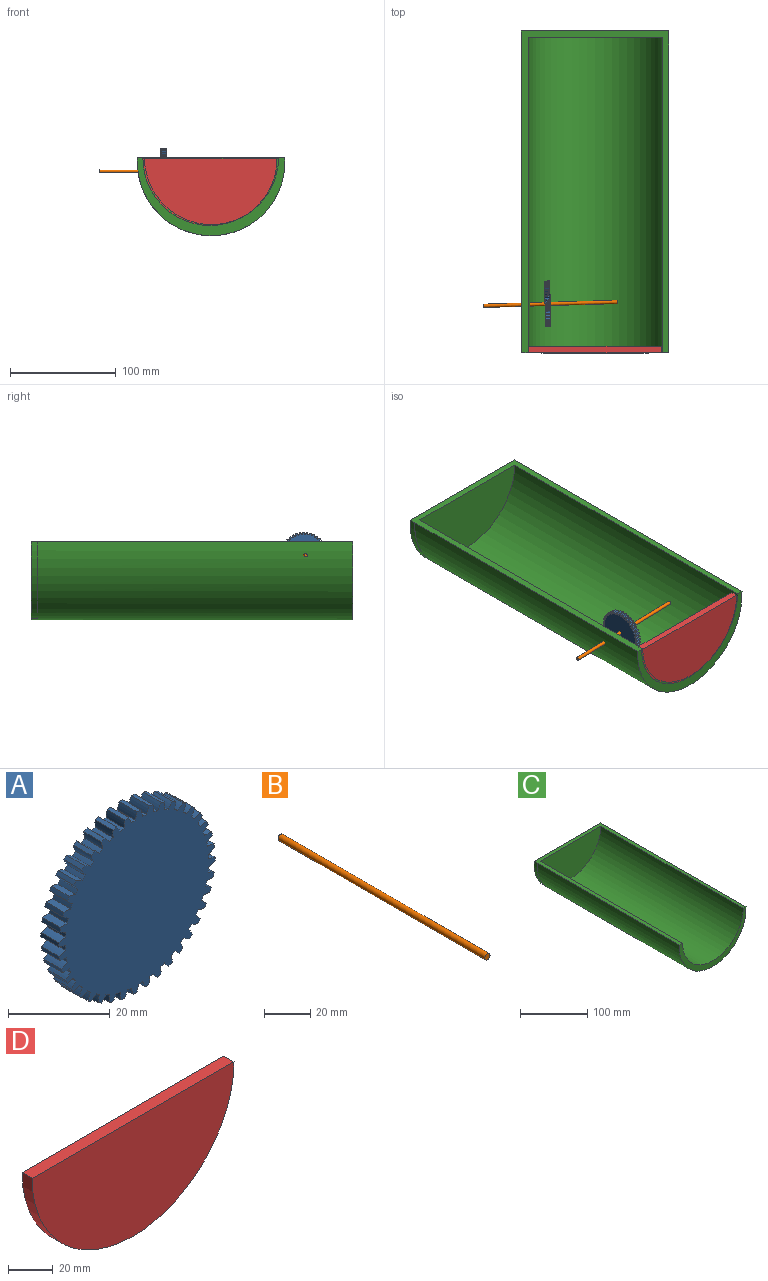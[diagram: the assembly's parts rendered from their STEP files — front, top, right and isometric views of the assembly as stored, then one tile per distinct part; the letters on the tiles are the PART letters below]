
ASSEMBLY  parts=4 mates=2
PART A: 162 faces, bbox 43.5x5x43.5 mm
  f0: cylinder r=20mm len=5mm, axis (0,1,0), area 5.8mm2, adj f40,f41,f42,f161
  f1: cylinder r=20mm len=5mm, axis (0,1,0), area 5.8mm2, adj f40,f41,f158,f159
  f2: cylinder r=20mm len=5mm, axis (0,1,0), area 5.8mm2, adj f40,f41,f155,f156
  f3: cylinder r=20mm len=5mm, axis (0,1,0), area 5.8mm2, adj f40,f41,f152,f153
  f4: cylinder r=20mm len=5mm, axis (0,1,0), area 5.8mm2, adj f40,f41,f149,f150
  f5: cylinder r=20mm len=5mm, axis (0,1,0), area 5.8mm2, adj f40,f41,f146,f147
  f6: cylinder r=20mm len=5mm, axis (0,1,0), area 5.8mm2, adj f40,f41,f143,f144
  f7: cylinder r=20mm len=5mm, axis (0,1,0), area 5.8mm2, adj f40,f41,f140,f141
  f8: cylinder r=20mm len=5mm, axis (0,1,0), area 5.8mm2, adj f40,f41,f137,f138
  f9: cylinder r=20mm len=5mm, axis (0,1,0), area 5.8mm2, adj f40,f41,f134,f135
  f10: cylinder r=20mm len=5mm, axis (0,1,0), area 5.8mm2, adj f40,f41,f131,f132
  f11: cylinder r=20mm len=5mm, axis (0,1,0), area 5.8mm2, adj f40,f41,f128,f129
  f12: cylinder r=20mm len=5mm, axis (0,1,0), area 5.8mm2, adj f40,f41,f125,f126
  f13: cylinder r=20mm len=5mm, axis (0,1,0), area 5.8mm2, adj f40,f41,f122,f123
  f14: cylinder r=20mm len=5mm, axis (0,1,0), area 5.8mm2, adj f40,f41,f119,f120
  f15: cylinder r=20mm len=5mm, axis (0,1,0), area 5.8mm2, adj f40,f41,f116,f117
  f16: cylinder r=20mm len=5mm, axis (0,1,0), area 5.8mm2, adj f40,f41,f113,f114
  f17: cylinder r=20mm len=5mm, axis (0,1,0), area 5.8mm2, adj f40,f41,f110,f111
  f18: cylinder r=20mm len=5mm, axis (0,1,0), area 5.8mm2, adj f40,f41,f107,f108
  f19: cylinder r=20mm len=5mm, axis (0,1,0), area 5.8mm2, adj f40,f41,f104,f105
  f20: cylinder r=20mm len=5mm, axis (0,1,0), area 5.8mm2, adj f40,f41,f101,f102
  f21: cylinder r=20mm len=5mm, axis (0,1,0), area 5.8mm2, adj f40,f41,f98,f99
  f22: cylinder r=20mm len=5mm, axis (0,1,0), area 5.8mm2, adj f40,f41,f95,f96
  f23: cylinder r=20mm len=5mm, axis (0,1,0), area 5.8mm2, adj f40,f41,f92,f93
  f24: cylinder r=20mm len=5mm, axis (0,1,0), area 5.8mm2, adj f40,f41,f89,f90
  f25: cylinder r=20mm len=5mm, axis (0,1,0), area 5.8mm2, adj f40,f41,f86,f87
  f26: cylinder r=20mm len=5mm, axis (0,1,0), area 5.8mm2, adj f40,f41,f83,f84
  f27: cylinder r=20mm len=5mm, axis (0,1,0), area 5.8mm2, adj f40,f41,f80,f81
  f28: cylinder r=20mm len=5mm, axis (0,1,0), area 5.8mm2, adj f40,f41,f77,f78
  f29: cylinder r=20mm len=5mm, axis (0,1,0), area 5.8mm2, adj f40,f41,f74,f75
  f30: cylinder r=20mm len=5mm, axis (0,1,0), area 5.8mm2, adj f40,f41,f71,f72
  f31: cylinder r=20mm len=5mm, axis (0,1,0), area 5.8mm2, adj f40,f41,f68,f69
  f32: cylinder r=20mm len=5mm, axis (0,1,0), area 5.8mm2, adj f40,f41,f65,f66
  f33: cylinder r=20mm len=5mm, axis (0,1,0), area 5.8mm2, adj f40,f41,f62,f63
  f34: cylinder r=20mm len=5mm, axis (0,1,0), area 5.8mm2, adj f40,f41,f59,f60
  f35: cylinder r=20mm len=5mm, axis (0,1,0), area 5.8mm2, adj f40,f41,f56,f57
  f36: cylinder r=20mm len=5mm, axis (0,1,0), area 5.8mm2, adj f40,f41,f53,f54
  f37: cylinder r=20mm len=5mm, axis (0,1,0), area 5.8mm2, adj f40,f41,f50,f51
  f38: cylinder r=20mm len=5mm, axis (0,1,0), area 5.8mm2, adj f40,f41,f47,f48
  f39: cylinder r=20mm len=5mm, axis (0,1,0), area 5.8mm2, adj f40,f41,f44,f45
  f40: plane 43.5x43.5mm, normal (0,-1,0), area 1366.6mm2, adj f0,f1,f2,f3,f4,f5,f6,f7
  f41: plane 43.5x43.5mm, normal (0,1,0), area 1366.6mm2, adj f0,f1,f2,f3,f4,f5,f6,f7
  f42: cylinder r=8.16mm len=5mm, axis (0,1,0), area 9.2mm2, adj f0,f40,f41,f43
  f43: cylinder r=21.75mm len=5mm, axis (0,1,0), area 5.1mm2, adj f40,f41,f42,f44
  f44: cylinder r=8.16mm len=5mm, axis (0,1,0), area 9.2mm2, adj f39,f40,f41,f43
  f45: cylinder r=8.16mm len=5mm, axis (0,1,0), area 9.2mm2, adj f39,f40,f41,f46
  f46: cylinder r=21.75mm len=5mm, axis (0,1,0), area 5.1mm2, adj f40,f41,f45,f47
  f47: cylinder r=8.16mm len=5mm, axis (0,1,0), area 9.2mm2, adj f38,f40,f41,f46
  f48: cylinder r=8.16mm len=5mm, axis (0,1,0), area 9.2mm2, adj f38,f40,f41,f49
  f49: cylinder r=21.75mm len=5mm, axis (0,1,0), area 5.1mm2, adj f40,f41,f48,f50
  f50: cylinder r=8.16mm len=5mm, axis (0,1,0), area 9.2mm2, adj f37,f40,f41,f49
  f51: cylinder r=8.16mm len=5mm, axis (0,1,0), area 9.2mm2, adj f37,f40,f41,f52
  f52: cylinder r=21.75mm len=5mm, axis (0,1,0), area 5.1mm2, adj f40,f41,f51,f53
  f53: cylinder r=8.16mm len=5mm, axis (0,1,0), area 9.2mm2, adj f36,f40,f41,f52
  f54: cylinder r=8.16mm len=5mm, axis (0,1,0), area 9.2mm2, adj f36,f40,f41,f55
  f55: cylinder r=21.75mm len=5mm, axis (0,1,0), area 5.1mm2, adj f40,f41,f54,f56
  f56: cylinder r=8.16mm len=5mm, axis (0,1,0), area 9.2mm2, adj f35,f40,f41,f55
  f57: cylinder r=8.16mm len=5mm, axis (0,1,0), area 9.2mm2, adj f35,f40,f41,f58
  f58: cylinder r=21.75mm len=5mm, axis (0,1,0), area 5.1mm2, adj f40,f41,f57,f59
  f59: cylinder r=8.16mm len=5mm, axis (0,1,0), area 9.2mm2, adj f34,f40,f41,f58
  f60: cylinder r=8.16mm len=5mm, axis (0,1,0), area 9.2mm2, adj f34,f40,f41,f61
  f61: cylinder r=21.75mm len=5mm, axis (0,1,0), area 5.1mm2, adj f40,f41,f60,f62
  f62: cylinder r=8.16mm len=5mm, axis (0,1,0), area 9.2mm2, adj f33,f40,f41,f61
  f63: cylinder r=8.16mm len=5mm, axis (0,1,0), area 9.2mm2, adj f33,f40,f41,f64
  f64: cylinder r=21.75mm len=5mm, axis (0,1,0), area 5.1mm2, adj f40,f41,f63,f65
  f65: cylinder r=8.16mm len=5mm, axis (0,1,0), area 9.2mm2, adj f32,f40,f41,f64
  f66: cylinder r=8.16mm len=5mm, axis (0,1,0), area 9.2mm2, adj f32,f40,f41,f67
  f67: cylinder r=21.75mm len=5mm, axis (0,1,0), area 5.1mm2, adj f40,f41,f66,f68
  f68: cylinder r=8.16mm len=5mm, axis (0,1,0), area 9.2mm2, adj f31,f40,f41,f67
  f69: cylinder r=8.16mm len=5mm, axis (0,1,0), area 9.2mm2, adj f31,f40,f41,f70
  f70: cylinder r=21.75mm len=5mm, axis (0,1,0), area 5.1mm2, adj f40,f41,f69,f71
  f71: cylinder r=8.16mm len=5mm, axis (0,1,0), area 9.2mm2, adj f30,f40,f41,f70
  f72: cylinder r=8.16mm len=5mm, axis (0,1,0), area 9.2mm2, adj f30,f40,f41,f73
  f73: cylinder r=21.75mm len=5mm, axis (0,1,0), area 5.1mm2, adj f40,f41,f72,f74
  f74: cylinder r=8.16mm len=5mm, axis (0,1,0), area 9.2mm2, adj f29,f40,f41,f73
  f75: cylinder r=8.16mm len=5mm, axis (0,1,0), area 9.2mm2, adj f29,f40,f41,f76
  f76: cylinder r=21.75mm len=5mm, axis (0,1,0), area 5.1mm2, adj f40,f41,f75,f77
  f77: cylinder r=8.16mm len=5mm, axis (0,1,0), area 9.2mm2, adj f28,f40,f41,f76
  f78: cylinder r=8.16mm len=5mm, axis (0,1,0), area 9.2mm2, adj f28,f40,f41,f79
  f79: cylinder r=21.75mm len=5mm, axis (0,1,0), area 5.1mm2, adj f40,f41,f78,f80
  f80: cylinder r=8.16mm len=5mm, axis (0,1,0), area 9.2mm2, adj f27,f40,f41,f79
  f81: cylinder r=8.16mm len=5mm, axis (0,1,0), area 9.2mm2, adj f27,f40,f41,f82
  f82: cylinder r=21.75mm len=5mm, axis (0,1,0), area 5.1mm2, adj f40,f41,f81,f83
  f83: cylinder r=8.16mm len=5mm, axis (0,1,0), area 9.2mm2, adj f26,f40,f41,f82
  f84: cylinder r=8.16mm len=5mm, axis (0,1,0), area 9.2mm2, adj f26,f40,f41,f85
  f85: cylinder r=21.75mm len=5mm, axis (0,1,0), area 5.1mm2, adj f40,f41,f84,f86
  f86: cylinder r=8.16mm len=5mm, axis (0,1,0), area 9.2mm2, adj f25,f40,f41,f85
  f87: cylinder r=8.16mm len=5mm, axis (0,1,0), area 9.2mm2, adj f25,f40,f41,f88
  f88: cylinder r=21.75mm len=5mm, axis (0,1,0), area 5.1mm2, adj f40,f41,f87,f89
  f89: cylinder r=8.16mm len=5mm, axis (0,1,0), area 9.2mm2, adj f24,f40,f41,f88
  f90: cylinder r=8.16mm len=5mm, axis (0,1,0), area 9.2mm2, adj f24,f40,f41,f91
  f91: cylinder r=21.75mm len=5mm, axis (0,1,0), area 5.1mm2, adj f40,f41,f90,f92
  f92: cylinder r=8.16mm len=5mm, axis (0,1,0), area 9.2mm2, adj f23,f40,f41,f91
  f93: cylinder r=8.16mm len=5mm, axis (0,1,0), area 9.2mm2, adj f23,f40,f41,f94
  f94: cylinder r=21.75mm len=5mm, axis (0,1,0), area 5.1mm2, adj f40,f41,f93,f95
  f95: cylinder r=8.16mm len=5mm, axis (0,1,0), area 9.2mm2, adj f22,f40,f41,f94
  f96: cylinder r=8.16mm len=5mm, axis (0,1,0), area 9.2mm2, adj f22,f40,f41,f97
  f97: cylinder r=21.75mm len=5mm, axis (0,1,0), area 5.1mm2, adj f40,f41,f96,f98
  f98: cylinder r=8.16mm len=5mm, axis (0,1,0), area 9.2mm2, adj f21,f40,f41,f97
  f99: cylinder r=8.16mm len=5mm, axis (0,1,0), area 9.2mm2, adj f21,f40,f41,f100
  f100: cylinder r=21.75mm len=5mm, axis (0,1,0), area 5.1mm2, adj f40,f41,f99,f101
  f101: cylinder r=8.16mm len=5mm, axis (0,1,0), area 9.2mm2, adj f20,f40,f41,f100
  f102: cylinder r=8.16mm len=5mm, axis (0,1,0), area 9.2mm2, adj f20,f40,f41,f103
  f103: cylinder r=21.75mm len=5mm, axis (0,1,0), area 5.1mm2, adj f40,f41,f102,f104
  f104: cylinder r=8.16mm len=5mm, axis (0,1,0), area 9.2mm2, adj f19,f40,f41,f103
  f105: cylinder r=8.16mm len=5mm, axis (0,1,0), area 9.2mm2, adj f19,f40,f41,f106
  f106: cylinder r=21.75mm len=5mm, axis (0,1,0), area 5.1mm2, adj f40,f41,f105,f107
  f107: cylinder r=8.16mm len=5mm, axis (0,1,0), area 9.2mm2, adj f18,f40,f41,f106
  f108: cylinder r=8.16mm len=5mm, axis (0,1,0), area 9.2mm2, adj f18,f40,f41,f109
  f109: cylinder r=21.75mm len=5mm, axis (0,1,0), area 5.1mm2, adj f40,f41,f108,f110
  f110: cylinder r=8.16mm len=5mm, axis (0,1,0), area 9.2mm2, adj f17,f40,f41,f109
  f111: cylinder r=8.16mm len=5mm, axis (0,1,0), area 9.2mm2, adj f17,f40,f41,f112
  f112: cylinder r=21.75mm len=5mm, axis (0,1,0), area 5.1mm2, adj f40,f41,f111,f113
  f113: cylinder r=8.16mm len=5mm, axis (0,1,0), area 9.2mm2, adj f16,f40,f41,f112
  f114: cylinder r=8.16mm len=5mm, axis (0,1,0), area 9.2mm2, adj f16,f40,f41,f115
  f115: cylinder r=21.75mm len=5mm, axis (0,1,0), area 5.1mm2, adj f40,f41,f114,f116
  f116: cylinder r=8.16mm len=5mm, axis (0,1,0), area 9.2mm2, adj f15,f40,f41,f115
  f117: cylinder r=8.16mm len=5mm, axis (0,1,0), area 9.2mm2, adj f15,f40,f41,f118
  f118: cylinder r=21.75mm len=5mm, axis (0,1,0), area 5.1mm2, adj f40,f41,f117,f119
  f119: cylinder r=8.16mm len=5mm, axis (0,1,0), area 9.2mm2, adj f14,f40,f41,f118
  f120: cylinder r=8.16mm len=5mm, axis (0,1,0), area 9.2mm2, adj f14,f40,f41,f121
  f121: cylinder r=21.75mm len=5mm, axis (0,1,0), area 5.1mm2, adj f40,f41,f120,f122
  f122: cylinder r=8.16mm len=5mm, axis (0,1,0), area 9.2mm2, adj f13,f40,f41,f121
  f123: cylinder r=8.16mm len=5mm, axis (0,1,0), area 9.2mm2, adj f13,f40,f41,f124
  f124: cylinder r=21.75mm len=5mm, axis (0,1,0), area 5.1mm2, adj f40,f41,f123,f125
  f125: cylinder r=8.16mm len=5mm, axis (0,1,0), area 9.2mm2, adj f12,f40,f41,f124
  f126: cylinder r=8.16mm len=5mm, axis (0,1,0), area 9.2mm2, adj f12,f40,f41,f127
  f127: cylinder r=21.75mm len=5mm, axis (0,1,0), area 5.1mm2, adj f40,f41,f126,f128
  f128: cylinder r=8.16mm len=5mm, axis (0,1,0), area 9.2mm2, adj f11,f40,f41,f127
  f129: cylinder r=8.16mm len=5mm, axis (0,1,0), area 9.2mm2, adj f11,f40,f41,f130
  f130: cylinder r=21.75mm len=5mm, axis (0,1,0), area 5.1mm2, adj f40,f41,f129,f131
  f131: cylinder r=8.16mm len=5mm, axis (0,1,0), area 9.2mm2, adj f10,f40,f41,f130
  f132: cylinder r=8.16mm len=5mm, axis (0,1,0), area 9.2mm2, adj f10,f40,f41,f133
  f133: cylinder r=21.75mm len=5mm, axis (0,1,0), area 5.1mm2, adj f40,f41,f132,f134
  f134: cylinder r=8.16mm len=5mm, axis (0,1,0), area 9.2mm2, adj f9,f40,f41,f133
  f135: cylinder r=8.16mm len=5mm, axis (0,1,0), area 9.2mm2, adj f9,f40,f41,f136
  f136: cylinder r=21.75mm len=5mm, axis (0,1,0), area 5.1mm2, adj f40,f41,f135,f137
  f137: cylinder r=8.16mm len=5mm, axis (0,1,0), area 9.2mm2, adj f8,f40,f41,f136
  f138: cylinder r=8.16mm len=5mm, axis (0,1,0), area 9.2mm2, adj f8,f40,f41,f139
  f139: cylinder r=21.75mm len=5mm, axis (0,1,0), area 5.1mm2, adj f40,f41,f138,f140
  f140: cylinder r=8.16mm len=5mm, axis (0,1,0), area 9.2mm2, adj f7,f40,f41,f139
  f141: cylinder r=8.16mm len=5mm, axis (0,1,0), area 9.2mm2, adj f7,f40,f41,f142
  f142: cylinder r=21.75mm len=5mm, axis (0,1,0), area 5.1mm2, adj f40,f41,f141,f143
  f143: cylinder r=8.16mm len=5mm, axis (0,1,0), area 9.2mm2, adj f6,f40,f41,f142
  f144: cylinder r=8.16mm len=5mm, axis (0,1,0), area 9.2mm2, adj f6,f40,f41,f145
  f145: cylinder r=21.75mm len=5mm, axis (0,1,0), area 5.1mm2, adj f40,f41,f144,f146
  f146: cylinder r=8.16mm len=5mm, axis (0,1,0), area 9.2mm2, adj f5,f40,f41,f145
  f147: cylinder r=8.16mm len=5mm, axis (0,1,0), area 9.2mm2, adj f5,f40,f41,f148
  f148: cylinder r=21.75mm len=5mm, axis (0,1,0), area 5.1mm2, adj f40,f41,f147,f149
  f149: cylinder r=8.16mm len=5mm, axis (0,1,0), area 9.2mm2, adj f4,f40,f41,f148
  f150: cylinder r=8.16mm len=5mm, axis (0,1,0), area 9.2mm2, adj f4,f40,f41,f151
  f151: cylinder r=21.75mm len=5mm, axis (0,1,0), area 5.1mm2, adj f40,f41,f150,f152
  f152: cylinder r=8.16mm len=5mm, axis (0,1,0), area 9.2mm2, adj f3,f40,f41,f151
  f153: cylinder r=8.16mm len=5mm, axis (0,1,0), area 9.2mm2, adj f3,f40,f41,f154
  f154: cylinder r=21.75mm len=5mm, axis (0,1,0), area 5.1mm2, adj f40,f41,f153,f155
  f155: cylinder r=8.16mm len=5mm, axis (0,1,0), area 9.2mm2, adj f2,f40,f41,f154
  f156: cylinder r=8.16mm len=5mm, axis (0,1,0), area 9.2mm2, adj f2,f40,f41,f157
  f157: cylinder r=21.75mm len=5mm, axis (0,1,0), area 5.1mm2, adj f40,f41,f156,f158
  f158: cylinder r=8.16mm len=5mm, axis (0,1,0), area 9.2mm2, adj f1,f40,f41,f157
  f159: cylinder r=8.16mm len=5mm, axis (0,1,0), area 9.2mm2, adj f1,f40,f41,f160
  f160: cylinder r=21.75mm len=5mm, axis (0,1,0), area 5.1mm2, adj f40,f41,f159,f161
  f161: cylinder r=8.16mm len=5mm, axis (0,1,0), area 9.2mm2, adj f0,f40,f41,f160
PART B: 3 faces, bbox 3.1x127x3.1 mm
  f0: cylinder r=1.57mm len=127mm, axis (0,1,0), area 1256.6mm2, adj f1,f2
  f1: plane 3.15x3.15mm, normal (0,-1,0), area 7.8mm2, adj f0
  f2: plane 3.15x3.15mm, normal (0,1,0), area 7.8mm2, adj f0
PART C: 8 faces, bbox 139.9x304.8x73.8 mm
  f0: cylinder r=69.85mm len=304.8mm, axis (0,1,0), area 68683.6mm2, adj f1,f3,f4,f6,f7
  f1: plane 304.8x139.71mm, normal (0,0,1), area 4609.9mm2, adj f0,f2,f3,f4,f5,f6,f7
  f2: cylinder r=63.5mm len=298.45mm, axis (0,1,0), area 59388.5mm2, adj f1,f3,f5
  f3: plane 139.7x73.84mm, normal (0,-1,0), area 1918.4mm2, adj f0,f1,f2
  f4: plane 139.94x73.84mm, normal (0,1,0), area 8234.9mm2, adj f0,f1,f6
  f5: plane 127x63.25mm, normal (0,-1,0), area 6302mm2, adj f1,f2
  f6: cylinder r=69.85mm len=72.42mm, axis (0,1,0), area 633.8mm2, adj f0,f1,f4,f7
  f7: plane 72.42x56.09mm, normal (0,-1,0), area 14.5mm2, adj f0,f1,f6
PART D: 4 faces, bbox 127x6.4x63.3 mm
  f0: plane 127x6.35mm, normal (0,0,1), area 806.4mm2, adj f1,f2,f3
  f1: cylinder r=63.5mm len=127mm, axis (0,1,0), area 1263.7mm2, adj f0,f2,f3
  f2: plane 127x63.26mm, normal (0,-1,0), area 6303.1mm2, adj f0,f1
  f3: plane 127x63.26mm, normal (0,1,0), area 6303.1mm2, adj f0,f1
PLACE A rot(axis=(0.72,-0.7,0),180deg) t=(-43.03,39.95,-117.71)mm
PLACE B rot(axis=(0,0,-1),88.4deg) t=(25.45,41.91,-117.71)mm
PLACE C t=(4.64,298.45,-104.85)mm
PLACE D t=(3.27,0,-105.74)mm
MATE fastened C.f3 <-> D.f2  axis (0,-1,0) through (3.35,-6.35,-151.63)mm
MATE fastened A.f0 <-> B.f0  axis (1,0.03,0) through (-38.03,40.09,-117.71)mm
